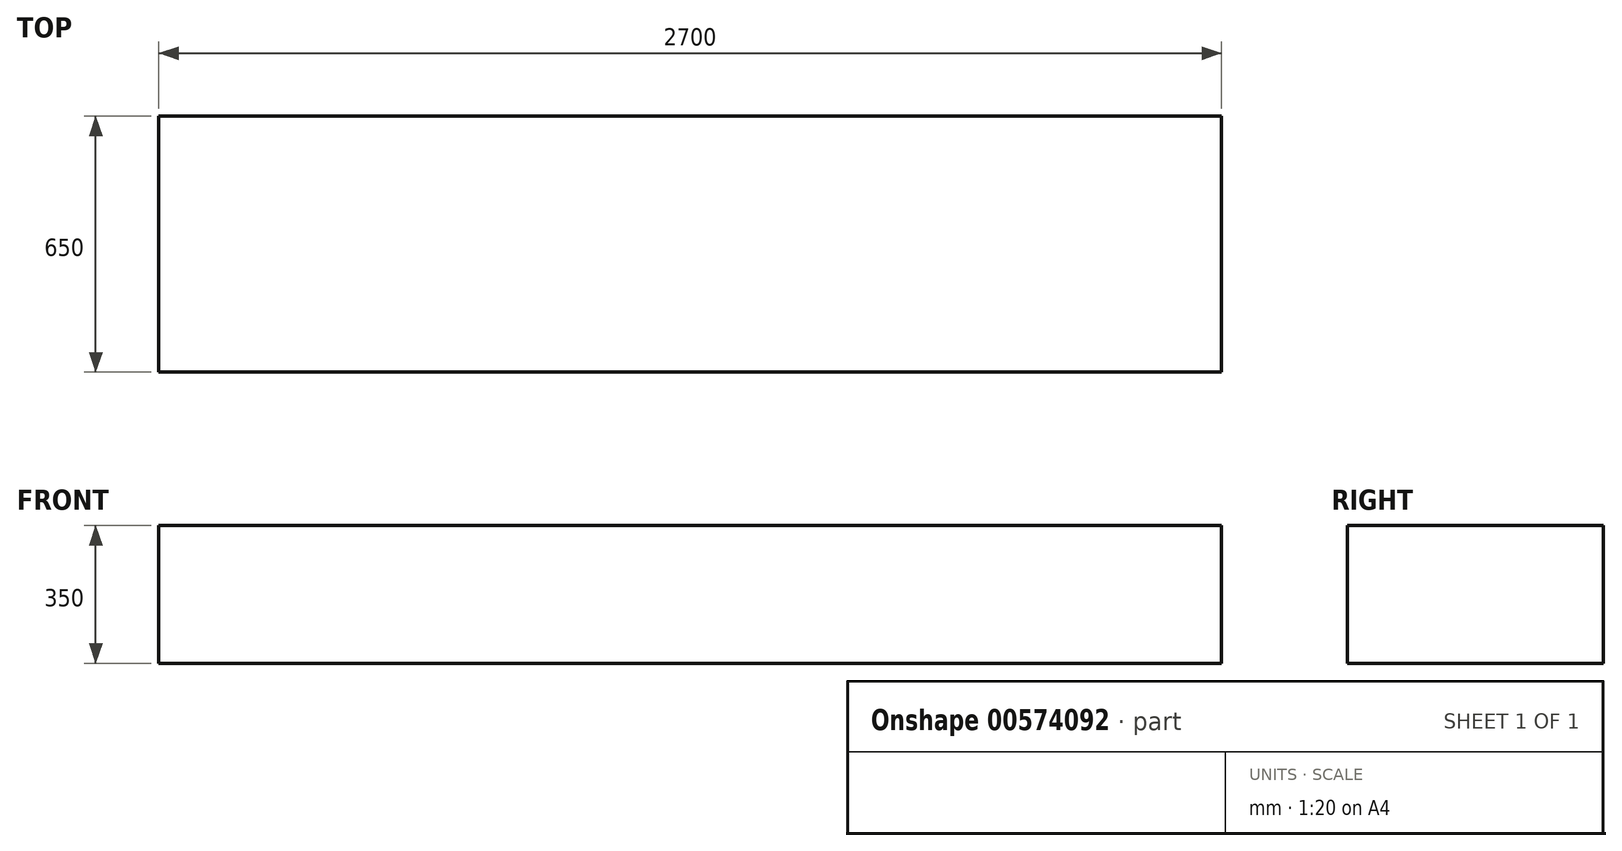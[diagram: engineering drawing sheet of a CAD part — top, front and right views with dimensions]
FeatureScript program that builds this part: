
annotation { "Feature Type Name" : "Feature", "Feature Type Description" : "" }
export const myFeature = defineFeature(function(context is Context, id is Id, definition is map)
    precondition{}
    {
        {
            var Q0;
            Q0=qCreatedBy(makeId("Top.planeOp"),FACE);
            var sketch = newSketch(context, id + "F0", { "sketchPlane" : qUnion([Q0])});
            skLineSegment(sketch, "E0.bottom", {"start": v(-1340.78, -419.6) * mm, "end": v(1359.22, -419.6) * mm});
            skLineSegment(sketch, "E0.top", {"start": v(-1340.78, -1069.6) * mm, "end": v(1359.22, -1069.6) * mm});
            skLineSegment(sketch, "E0.left", {"start": v(-1340.78, -419.6) * mm, "end": v(-1340.78, -1069.6) * mm});
            skLineSegment(sketch, "E0.right", {"start": v(1359.22, -419.6) * mm, "end": v(1359.22, -1069.6) * mm});
            skSolve(sketch);
        }
        {
            var Q0;
            Q0=makeQuery(id+"F0.imprint","IMPRINT",FACE,{"disambiguationData":[TD([[makeQuery(id+"F0.imprint","IMPRINT",EDGE,{"derivedFrom":sQuery(id+"F0.wireOp",EDGE,"E0.bottom")}),-1.0]])]});
            extrude(context, id + "F1", {"entities" : qUnion([Q0]), "depth" : 350 * mm, "offsetDistance" : 25 * mm});
        }
    });
